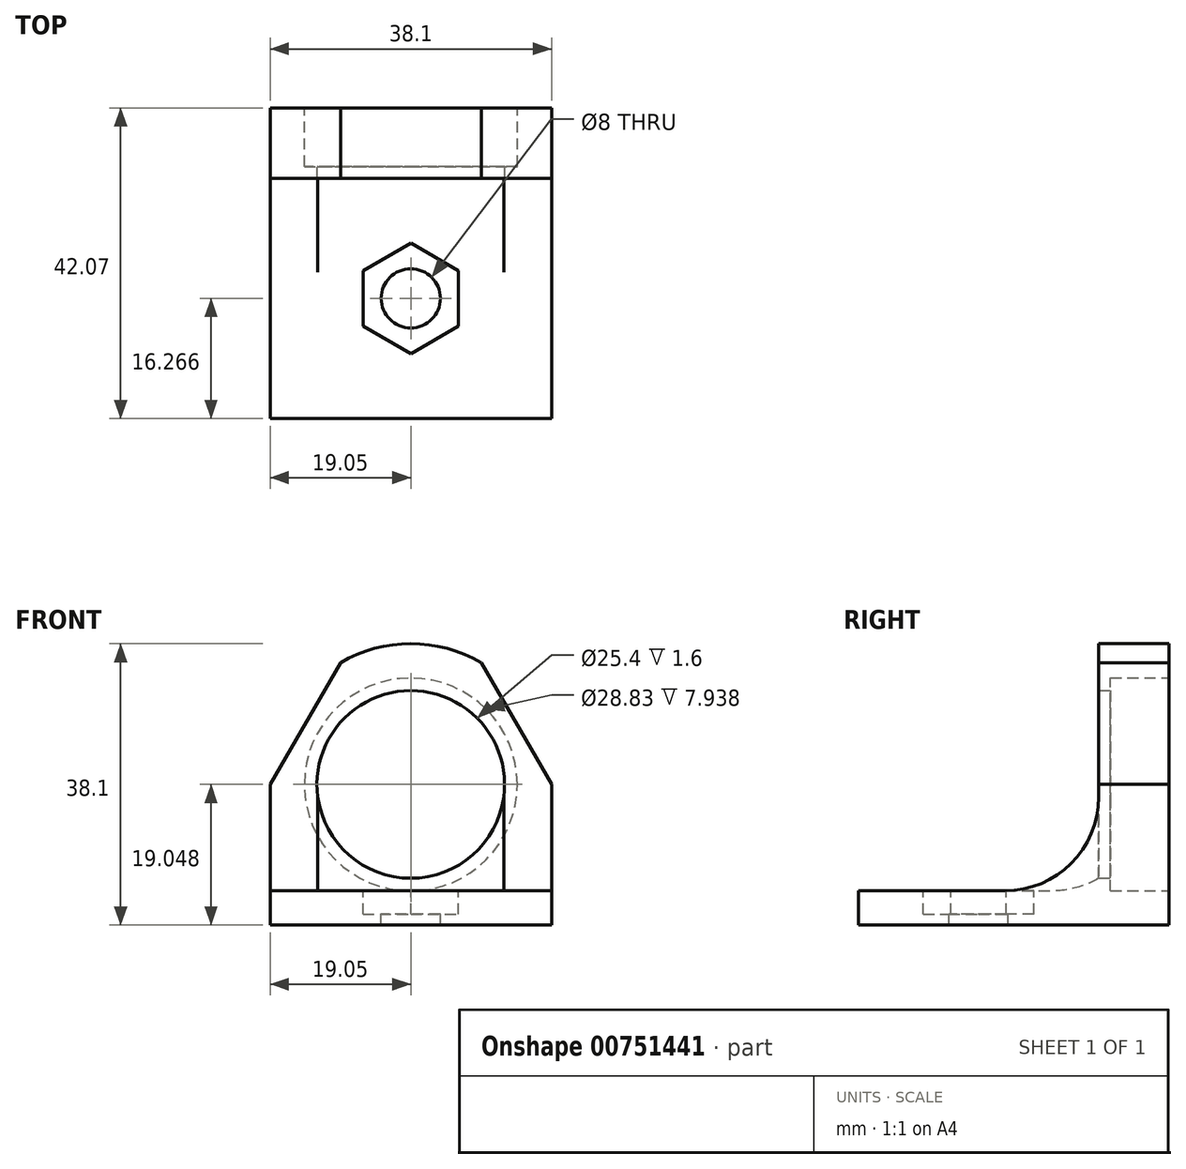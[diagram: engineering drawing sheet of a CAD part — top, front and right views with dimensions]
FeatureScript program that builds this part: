
annotation { "Feature Type Name" : "Feature", "Feature Type Description" : "" }
export const myFeature = defineFeature(function(context is Context, id is Id, definition is map)
    precondition{}
    {
        {
            var Q0;
            Q0=qCreatedBy(makeId("Front.planeOp"),FACE);
            var sketch = newSketch(context, id + "F0", { "sketchPlane" : qUnion([Q0])});
            skLineSegment(sketch, "E0.bottom", {"start": v(-38.1, 15.06) * mm, "end": v(38.1, 15.06) * mm, "construction": true});
            skLineSegment(sketch, "E0.top", {"start": v(-38.1, -15.06) * mm, "end": v(38.1, -15.06) * mm, "construction": true});
            skLineSegment(sketch, "E0.left", {"start": v(-38.1, 15.06) * mm, "end": v(-38.1, -15.06) * mm, "construction": true});
            skLineSegment(sketch, "E0.right", {"start": v(38.1, 15.06) * mm, "end": v(38.1, -15.06) * mm, "construction": true});
            skPoint(sketch, "E1", {"position": v(-38.1, 0) * mm});
            skPoint(sketch, "E2", {"position": v(0, 15.06) * mm});
            skCircle(sketch, "E3", {"center": v(-28.57, 1.45) * mm, "radius": 4.76 * mm, "construction": true});
            skArc(sketch, "E4", {"start": v(-11.11, 6.21) * mm, "mid": v(-15.88, 1.45) * mm, "end": v(-11.11, -3.31) * mm, "construction": true});
            skArc(sketch, "E5", {"start": v(-7.94, -3.31) * mm, "mid": v(-3.17, 1.45) * mm, "end": v(-7.94, 6.21) * mm, "construction": true});
            skLineSegment(sketch, "E6", {"start": v(-11.11, 6.21) * mm, "end": v(-7.94, 6.21) * mm, "construction": true});
            skLineSegment(sketch, "E7", {"start": v(-11.11, -3.31) * mm, "end": v(-7.94, -3.31) * mm, "construction": true});
            skArc(sketch, "E8", {"start": v(7.94, 6.21) * mm, "mid": v(3.18, 1.45) * mm, "end": v(7.94, -3.31) * mm, "construction": true});
            skArc(sketch, "E9", {"start": v(11.11, -3.31) * mm, "mid": v(15.88, 1.45) * mm, "end": v(11.11, 6.21) * mm, "construction": true});
            skLineSegment(sketch, "E10", {"start": v(7.94, 6.21) * mm, "end": v(11.11, 6.21) * mm, "construction": true});
            skLineSegment(sketch, "E11", {"start": v(7.94, -3.31) * mm, "end": v(11.11, -3.31) * mm, "construction": true});
            skCircle(sketch, "E12", {"center": v(28.57, 1.45) * mm, "radius": 4.76 * mm, "construction": true});
            skLineSegment(sketch, "E13.top", {"start": v(-38.1, -13.7) * mm, "end": v(38.1, -13.7) * mm, "construction": true});
            skLineSegment(sketch, "E13.left", {"start": v(-38.1, -15.06) * mm, "end": v(-38.1, -13.7) * mm, "construction": true});
            skLineSegment(sketch, "E13.right", {"start": v(38.1, -15.06) * mm, "end": v(38.1, -13.7) * mm, "construction": true});
            skCircle(sketch, "E14", {"center": v(0, 3.99) * mm, "radius": 6.35 * mm, "construction": true});
            skCircle(sketch, "E15", {"center": v(0, 3.99) * mm, "radius": 14.29 * mm, "construction": true});
            skCircle(sketch, "E16", {"center": v(0, 3.99) * mm, "radius": 50.8 * mm, "construction": true});
            skPoint(sketch, "E17", {"position": v(-9.52, 6.21) * mm});
            skPoint(sketch, "E18", {"position": v(-9.52, -3.31) * mm});
            skPoint(sketch, "E19", {"position": v(9.53, 6.21) * mm});
            skPoint(sketch, "E20", {"position": v(9.53, -3.31) * mm});
            skSolve(sketch);
        }
        {
            var Q0;
            Q0=qCreatedBy(makeId("Front.planeOp"),FACE);
            var sketch = newSketch(context, id + "F1", { "sketchPlane" : qUnion([Q0])});
            skArc(sketch, "E21", {"start": v(9.52, 20.49) * mm, "mid": v(0, 23.04) * mm, "end": v(-9.53, 20.49) * mm});
            skCircle(sketch, "E22", {"center": v(0, 3.99) * mm, "radius": 14.41 * mm});
            skLineSegment(sketch, "E23.top", {"start": v(-19.05, -15.06) * mm, "end": v(19.05, -15.06) * mm});
            skLineSegment(sketch, "E23.left", {"start": v(-19.05, 3.99) * mm, "end": v(-19.05, -15.06) * mm});
            skLineSegment(sketch, "E23.right", {"start": v(19.05, 3.99) * mm, "end": v(19.05, -15.06) * mm});
            skLineSegment(sketch, "E24.bottom", {"start": v(-19.05, -10.43) * mm, "end": v(19.05, -10.43) * mm});
            skLineSegment(sketch, "E24.left", {"start": v(-19.05, -10.43) * mm, "end": v(-19.05, -15.06) * mm});
            skLineSegment(sketch, "E24.right", {"start": v(19.05, -10.43) * mm, "end": v(19.05, -15.06) * mm});
            skCircle(sketch, "E25", {"center": v(0, 3.99) * mm, "radius": 12.7 * mm});
            skLineSegment(sketch, "E26", {"start": v(-9.53, 20.49) * mm, "end": v(-19.05, 3.99) * mm});
            skLineSegment(sketch, "E27", {"start": v(19.05, 3.99) * mm, "end": v(9.52, 20.49) * mm});
            skSolve(sketch);
        }
        {
            var Q0;
            Q0=makeQuery(id+"F1.imprint","IMPRINT",FACE,{"disambiguationData":[TD([[makeQuery(id+"F1.imprint","IMPRINT",EDGE,{"derivedFrom":sQuery(id+"F1.wireOp",EDGE,"E21")}),1.0]])]});
            var Q1;
            Q1=makeQuery(id+"F1.imprint","IMPRINT",FACE,{"disambiguationData":[TD([[makeQuery(id+"F1.imprint","IMPRINT",EDGE,{"derivedFrom":sQuery(id+"F1.wireOp",EDGE,"E23.top")}),1.0]])]});
            extrude(context, id + "F2", {"entities" : qUnion([Q0, Q1]), "depth" : 5.57 * mm, "offsetDistance" : 25.4 * mm});
        }
        {
            var Q0;
            Q0=makeQuery(id+"F1.imprint","IMPRINT",FACE,{"disambiguationData":[TD([[makeQuery(id+"F1.imprint","IMPRINT",EDGE,{"derivedFrom":sQuery(id+"F1.wireOp",EDGE,"E22")}),1.0]])]});
            var Q1;
            Q1=makeQuery(id+"F2.opExtrude","CAP_FACE",FACE,{"disambiguationData":[OSD([sQuery(id+"F1.wireOp",EDGE,"E21"),sQuery(id+"F1.wireOp",EDGE,"E22"),sQuery(id+"F1.wireOp",EDGE,"E23.left"),sQuery(id+"F1.wireOp",EDGE,"E23.right"),sQuery(id+"F1.wireOp",EDGE,"E23.top"),sQuery(id+"F1.wireOp",EDGE,"E24.left"),sQuery(id+"F1.wireOp",EDGE,"E24.right")])],"isStart":false});
            extrude(context, id + "F3", {"entities" : qUnion([Q0]), "operationType" : NewBodyOperationType.ADD, "endBound" : BoundingType.UP_TO_SURFACE, "depth" : 25.4 * mm, "endBoundEntityFace" : qUnion([Q1]), "offsetDistance" : 25.4 * mm});
        }
        {
            var Q0;
            Q0=makeQuery(id+"F1.imprint","IMPRINT",FACE,{"disambiguationData":[TD([[makeQuery(id+"F1.imprint","IMPRINT",EDGE,{"derivedFrom":sQuery(id+"F1.wireOp",EDGE,"E22")}),1.0]])]});
            extrude(context, id + "F4", {"entities" : qUnion([Q0]), "operationType" : NewBodyOperationType.REMOVE, "depth" : 3.97 * mm, "offsetDistance" : 25.4 * mm});
        }
        {
            var Q0;
            Q0=makeQuery(id+"F1.imprint","IMPRINT",FACE,{"disambiguationData":[TD([[makeQuery(id+"F1.imprint","IMPRINT",EDGE,{"derivedFrom":sQuery(id+"F1.wireOp",EDGE,"E23.top")}),1.0]])]});
            extrude(context, id + "F5", {"entities" : qUnion([Q0]), "operationType" : NewBodyOperationType.ADD, "depth" : 38.1 * mm, "offsetDistance" : 25.4 * mm});
        }
        {
            var Q0;
            Q0=makeQuery(id+"F5.opExtrude","SWEPT_FACE",FACE,{"disambiguationData":[OSD([sQuery(id+"F1.wireOp",EDGE,"E24.bottom")])]});
            var sketch = newSketch(context, id + "F6", { "sketchPlane" : qUnion([Q0])});
            skLineSegment(sketch, "E28", {"start": v(0, -5.57) * mm, "end": v(0, -38.1) * mm, "construction": true});
            skPoint(sketch, "E28.startSnap0", {"position": v(0, -5.57) * mm});
            skCircle(sketch, "E29", {"center": v(0, -21.83) * mm, "radius": 4 * mm});
            skCircle(sketch, "E30.cCircle", {"center": v(0, -21.83) * mm, "radius": 6.48 * mm, "construction": true});
            skLineSegment(sketch, "E30.0", {"start": v(6.48, -18.1) * mm, "end": v(6.48, -25.57) * mm});
            skLineSegment(sketch, "E30.1", {"start": v(6.48, -25.57) * mm, "end": v(0, -29.31) * mm});
            skLineSegment(sketch, "E30.2", {"start": v(0, -29.31) * mm, "end": v(-6.48, -25.57) * mm});
            skLineSegment(sketch, "E30.3", {"start": v(-6.48, -25.57) * mm, "end": v(-6.48, -18.1) * mm});
            skLineSegment(sketch, "E30.4", {"start": v(-6.48, -18.1) * mm, "end": v(0, -14.36) * mm});
            skLineSegment(sketch, "E30.5", {"start": v(0, -14.36) * mm, "end": v(6.48, -18.1) * mm});
            skPoint(sketch, "E30.0.midPoint", {"position": v(6.48, -21.83) * mm});
            skSolve(sketch);
        }
        {
            var Q0;
            Q0=makeQuery(id+"F6.imprint","IMPRINT",FACE,{"disambiguationData":[TD([[makeQuery(id+"F6.imprint","IMPRINT",EDGE,{"derivedFrom":sQuery(id+"F6.wireOp",EDGE,"E29")}),-1.0]])]});
            extrude(context, id + "F7", {"entities" : qUnion([Q0]), "operationType" : NewBodyOperationType.REMOVE, "oppositeDirection" : true, "depth" : 3.17 * mm, "offsetDistance" : 25.4 * mm});
        }
        {
            var Q0;
            Q0=makeQuery(id+"F6.imprint","IMPRINT",FACE,{"disambiguationData":[TD([[makeQuery(id+"F6.imprint","IMPRINT",EDGE,{"derivedFrom":sQuery(id+"F6.wireOp",EDGE,"E29")}),1.0]])]});
            extrude(context, id + "F8", {"entities" : qUnion([Q0]), "operationType" : NewBodyOperationType.REMOVE, "endBound" : BoundingType.THROUGH_ALL, "oppositeDirection" : true, "depth" : 25.4 * mm, "offsetDistance" : 25.4 * mm});
        }
        {
            var Q0;
            {var subQ0=sQuery(id+"F1.wireOp",EDGE,"E22");Q0=makeQuery(id+"F5.boolean.opBoolean","INTERSECT",EDGE,{"derivedFrom":[makeQuery(id+"F3.boolean.opBoolean","MERGE",FACE,{"derivedFrom":[makeQuery(id+"F2.opExtrude","CAP_FACE",FACE,{"disambiguationData":[OSD([sQuery(id+"F1.wireOp",EDGE,"E21"),subQ0,sQuery(id+"F1.wireOp",EDGE,"E23.left"),sQuery(id+"F1.wireOp",EDGE,"E23.right"),sQuery(id+"F1.wireOp",EDGE,"E23.top"),sQuery(id+"F1.wireOp",EDGE,"E24.left"),sQuery(id+"F1.wireOp",EDGE,"E24.right"),sQuery(id+"F1.wireOp",EDGE,"E26"),sQuery(id+"F1.wireOp",EDGE,"E27")])],"isStart":false}),makeQuery(id+"F3.opExtrude","CAP_FACE",FACE,{"disambiguationData":[OSD([subQ0,sQuery(id+"F1.wireOp",EDGE,"E25")])],"isStart":false})]}),makeQuery(id+"F5.opExtrude","SWEPT_FACE",FACE,{"disambiguationData":[OSD([sQuery(id+"F1.wireOp",EDGE,"E24.bottom")])]})]});}
            fillet(context, id + "F9", {"entities" : qUnion([Q0]), "radius" : 12.7 * mm, "tangentPropagation" : true, "allowEdgeOverflow" : false});
        }
        {
            var Q0;
            {var subQ0=sQuery(id+"F1.wireOp",EDGE,"E22");Q0=makeQuery(id+"F3.boolean.opBoolean","MERGE",FACE,{"derivedFrom":[makeQuery(id+"F2.opExtrude","CAP_FACE",FACE,{"disambiguationData":[OSD([sQuery(id+"F1.wireOp",EDGE,"E21"),subQ0,sQuery(id+"F1.wireOp",EDGE,"E23.left"),sQuery(id+"F1.wireOp",EDGE,"E23.right"),sQuery(id+"F1.wireOp",EDGE,"E23.top"),sQuery(id+"F1.wireOp",EDGE,"E24.left"),sQuery(id+"F1.wireOp",EDGE,"E24.right"),sQuery(id+"F1.wireOp",EDGE,"E26"),sQuery(id+"F1.wireOp",EDGE,"E27")])],"isStart":true}),makeQuery(id+"F3.opExtrude","CAP_FACE",FACE,{"disambiguationData":[OSD([subQ0,sQuery(id+"F1.wireOp",EDGE,"E25")])],"isStart":true})]});}
            extrude(context, id + "F10", {"entities" : qUnion([Q0]), "operationType" : NewBodyOperationType.ADD, "depth" : 3.97 * mm, "offsetDistance" : 25.4 * mm});
        }
    });
